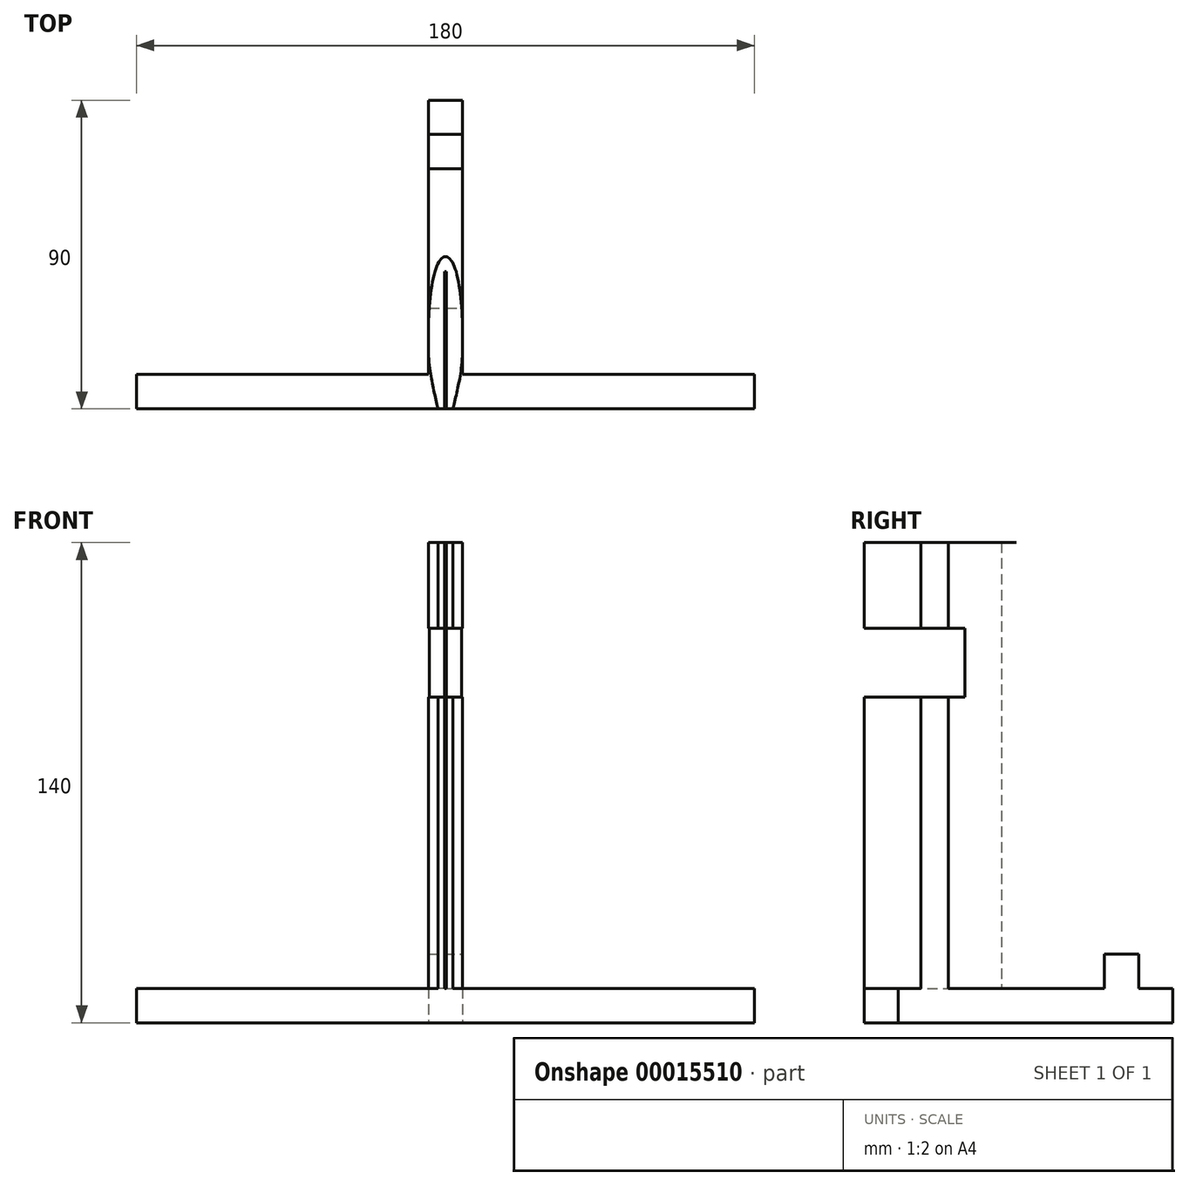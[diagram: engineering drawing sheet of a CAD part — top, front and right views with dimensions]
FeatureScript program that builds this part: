
annotation { "Feature Type Name" : "Feature", "Feature Type Description" : "" }
export const myFeature = defineFeature(function(context is Context, id is Id, definition is map)
    precondition{}
    {
        {
            var Q0;
            Q0=qCreatedBy(makeId("Top.planeOp"),FACE);
            var sketch = newSketch(context, id + "F0", { "sketchPlane" : qUnion([Q0])});
            skLineSegment(sketch, "E0", {"start": v(0, 90) * mm, "end": v(5, 90) * mm});
            skLineSegment(sketch, "E1", {"start": v(5, 90) * mm, "end": v(5, 10) * mm});
            skLineSegment(sketch, "E2", {"start": v(5, 10) * mm, "end": v(90, 10) * mm});
            skLineSegment(sketch, "E3", {"start": v(90, 10) * mm, "end": v(90, 0) * mm});
            skLineSegment(sketch, "E4", {"start": v(90, 0) * mm, "end": v(0, 0) * mm});
            skLineSegment(sketch, "E5.MirrorCS", {"start": v(0, 90) * mm, "end": v(-5, 90) * mm});
            skLineSegment(sketch, "E6.MirrorCS", {"start": v(-5, 90) * mm, "end": v(-5, 10) * mm});
            skLineSegment(sketch, "E7.MirrorCS", {"start": v(-5, 10) * mm, "end": v(-90, 10) * mm});
            skLineSegment(sketch, "E8.MirrorCS", {"start": v(-90, 10) * mm, "end": v(-90, 0) * mm});
            skLineSegment(sketch, "E9.MirrorCS", {"start": v(-90, 0) * mm, "end": v(0, 0) * mm});
            skSolve(sketch);
        }
        {
            var Q0;
            Q0=makeQuery(id+"F0.imprint","IMPRINT",FACE,{"disambiguationData":[TD([[makeQuery(id+"F0.imprint","IMPRINT",EDGE,{"derivedFrom":sQuery(id+"F0.wireOp",EDGE,"E0")}),-1.0]])]});
            extrude(context, id + "F1", {"entities" : qUnion([Q0]), "depth" : 10 * mm});
        }
        {
            var Q0;
            Q0=makeQuery(id+"F1.opExtrude","CAP_FACE",FACE,{"disambiguationData":[OSD([sQuery(id+"F0.wireOp",EDGE,"E0"),sQuery(id+"F0.wireOp",EDGE,"E1"),sQuery(id+"F0.wireOp",EDGE,"E2"),sQuery(id+"F0.wireOp",EDGE,"E3"),sQuery(id+"F0.wireOp",EDGE,"E4"),sQuery(id+"F0.wireOp",EDGE,"E5.MirrorCS"),sQuery(id+"F0.wireOp",EDGE,"E6.MirrorCS"),sQuery(id+"F0.wireOp",EDGE,"E7.MirrorCS"),sQuery(id+"F0.wireOp",EDGE,"E8.MirrorCS"),sQuery(id+"F0.wireOp",EDGE,"E9.MirrorCS")])],"isStart":false});
            var sketch = newSketch(context, id + "F2", { "sketchPlane" : qUnion([Q0])});
            skLineSegment(sketch, "E10.bottom", {"start": v(-5, 80) * mm, "end": v(5, 80) * mm});
            skLineSegment(sketch, "E10.top", {"start": v(-5, 70) * mm, "end": v(5, 70) * mm});
            skLineSegment(sketch, "E10.left", {"start": v(-5, 80) * mm, "end": v(-5, 70) * mm});
            skLineSegment(sketch, "E10.right", {"start": v(5, 80) * mm, "end": v(5, 70) * mm});
            skSolve(sketch);
        }
        {
            var Q0;
            Q0=makeQuery(id+"F2.imprint","IMPRINT",FACE,{"disambiguationData":[TD([[makeQuery(id+"F2.imprint","IMPRINT",EDGE,{"derivedFrom":sQuery(id+"F2.wireOp",EDGE,"E10.bottom")}),-1.0]])]});
            extrude(context, id + "F3", {"entities" : qUnion([Q0]), "operationType" : NewBodyOperationType.ADD, "depth" : 10 * mm});
        }
        {
            var Q0;
            {var subQ0=sQuery(id+"F0.wireOp",EDGE,"E1");var subQ1=sQuery(id+"F0.wireOp",EDGE,"E2");var subQ2=sQuery(id+"F0.wireOp",EDGE,"E3");var subQ3=sQuery(id+"F0.wireOp",EDGE,"E4");var subQ4=sQuery(id+"F0.wireOp",EDGE,"E6.MirrorCS");var subQ5=sQuery(id+"F0.wireOp",EDGE,"E7.MirrorCS");var subQ6=sQuery(id+"F0.wireOp",EDGE,"E8.MirrorCS");var subQ7=sQuery(id+"F0.wireOp",EDGE,"E9.MirrorCS");Q0=makeQuery(id+"F3.boolean.opBoolean","SPLIT",FACE,{"disambiguationData":[TD([makeQuery(id+"F1.opExtrude","SWEPT_FACE",FACE,{"disambiguationData":[OSD([subQ1])]})])],"derivedFrom":makeQuery(id+"F1.opExtrude","CAP_FACE",FACE,{"disambiguationData":[OSD([sQuery(id+"F0.wireOp",EDGE,"E0"),subQ0,subQ1,subQ2,subQ3,sQuery(id+"F0.wireOp",EDGE,"E5.MirrorCS"),subQ4,subQ5,subQ6,subQ7])],"isStart":false})});}
            var sketch = newSketch(context, id + "F4", { "sketchPlane" : qUnion([Q0])});
            skFitSpline(sketch, "E11", {"points": [v(0, 44.34) * mm, v(2.8, 40.95) * mm, v(5, 16.6) * mm, v(3.55, 6.02) * mm, v(2.2, 0) * mm], "startDerivative": vector(17.44, -0.09) * mm, "endDerivative": vector(-5.28, -21) * mm});
            skLineSegment(sketch, "E12", {"start": v(0, 44.34) * mm, "end": v(0, 24.79) * mm, "construction": true});
            skLineSegment(sketch, "E13", {"start": v(2.2, 0) * mm, "end": v(0.25, 0) * mm});
            skLineSegment(sketch, "E14", {"start": v(0.25, 0) * mm, "end": v(0.25, 40) * mm});
            skLineSegment(sketch, "E15", {"start": v(0.25, 40) * mm, "end": v(0, 40) * mm});
            skFitSpline(sketch, "E16.MirrorCS", {"points": [v(0, 44.34) * mm, v(-2.8, 40.95) * mm, v(-5, 16.6) * mm, v(-3.55, 6.02) * mm, v(-2.2, 0) * mm], "startDerivative": vector(-17.44, -0.09) * mm, "endDerivative": vector(5.28, -21) * mm});
            skLineSegment(sketch, "E17.MirrorCS", {"start": v(-0.25, 40) * mm, "end": v(0, 40) * mm});
            skLineSegment(sketch, "E18.MirrorCS", {"start": v(-0.25, 0) * mm, "end": v(-0.25, 40) * mm});
            skLineSegment(sketch, "E19.MirrorCS", {"start": v(-2.2, 0) * mm, "end": v(-0.25, 0) * mm});
            skSolve(sketch);
        }
        {
            var Q0;
            {var subQ19=sQuery(id+"F4.wireOp",EDGE,"E13");Q0=makeQuery(id+"F4.imprint","IMPRINT",FACE,{"disambiguationData":[TD([[makeQuery(id+"F4.imprint","IMPRINT",EDGE,{"derivedFrom":subQ19}),1.0]])]});}
            extrude(context, id + "F5", {"entities" : qUnion([Q0]), "operationType" : NewBodyOperationType.ADD, "depth" : 130 * mm});
        }
        {
            var Q0;
            Q0=qCreatedBy(makeId("Right.planeOp"),FACE);
            var sketch = newSketch(context, id + "F6", { "sketchPlane" : qUnion([Q0])});
            skLineSegment(sketch, "E20.bottom", {"start": v(-13.73, 95) * mm, "end": v(29.34, 95) * mm});
            skLineSegment(sketch, "E20.top", {"start": v(-13.73, 115) * mm, "end": v(29.34, 115) * mm});
            skLineSegment(sketch, "E20.left", {"start": v(-13.73, 95) * mm, "end": v(-13.73, 115) * mm});
            skLineSegment(sketch, "E20.right", {"start": v(29.34, 95) * mm, "end": v(29.34, 115) * mm});
            skSolve(sketch);
        }
        {
            var Q0;
            Q0=makeQuery(id+"F6.imprint","IMPRINT",FACE,{"disambiguationData":[TD([[makeQuery(id+"F6.imprint","IMPRINT",EDGE,{"derivedFrom":sQuery(id+"F6.wireOp",EDGE,"E20.bottom")}),1.0]])]});
            extrude(context, id + "F7", {"entities" : qUnion([Q0]), "operationType" : NewBodyOperationType.REMOVE, "endBound" : BoundingType.THROUGH_ALL, "oppositeDirection" : true, "depth" : 25 * mm, "hasSecondDirection" : true, "secondDirectionBound" : SecondDirectionBoundingType.THROUGH_ALL, "secondDirectionOppositeDirection" : false, "secondDirectionDepth" : 25 * mm});
        }
    });
